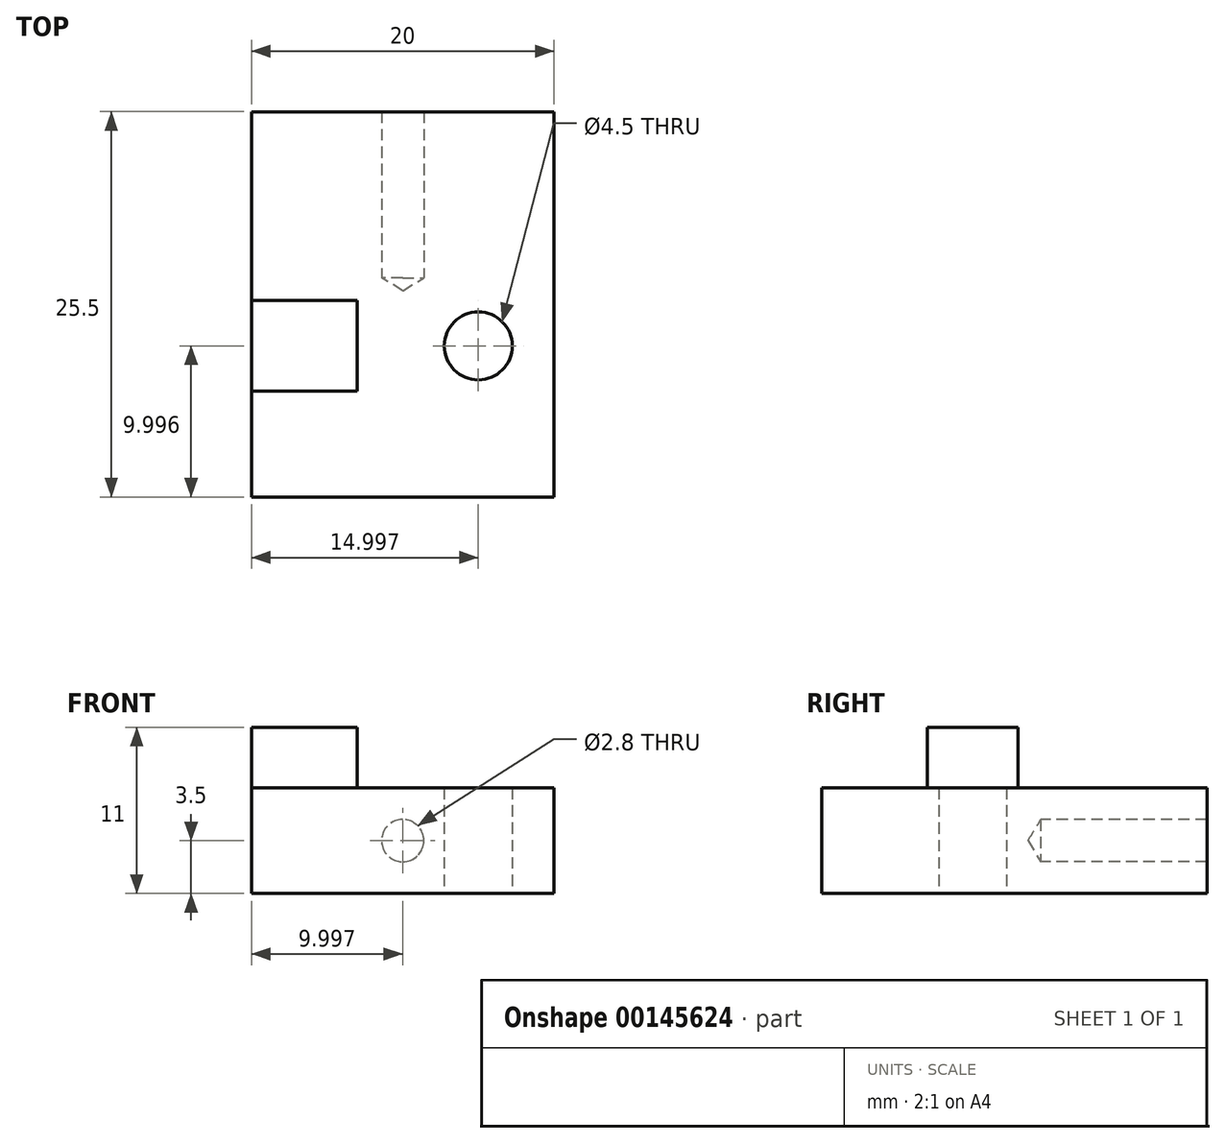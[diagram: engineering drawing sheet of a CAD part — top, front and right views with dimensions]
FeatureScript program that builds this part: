
annotation { "Feature Type Name" : "Feature", "Feature Type Description" : "" }
export const myFeature = defineFeature(function(context is Context, id is Id, definition is map)
    precondition{}
    {
        {
            var Q0;
            Q0=qCreatedBy(makeId("Top.planeOp"),FACE);
            var sketch = newSketch(context, id + "F0", { "sketchPlane" : qUnion([Q0])});
            skLineSegment(sketch, "E0.bottom", {"start": v(-42.58, 30.69) * mm, "end": v(-22.58, 30.69) * mm});
            skLineSegment(sketch, "E0.top", {"start": v(-42.58, 5.19) * mm, "end": v(-22.58, 5.19) * mm});
            skLineSegment(sketch, "E0.left", {"start": v(-42.58, 30.69) * mm, "end": v(-42.58, 5.19) * mm});
            skLineSegment(sketch, "E0.right", {"start": v(-22.58, 30.69) * mm, "end": v(-22.58, 5.19) * mm});
            skLineSegment(sketch, "E1", {"start": v(-41.58, 15.19) * mm, "end": v(-22.96, 15.19) * mm, "construction": true});
            skPoint(sketch, "E2", {"position": v(-39.08, 15.19) * mm});
            skPoint(sketch, "E3", {"position": v(-27.58, 15.19) * mm});
            skLineSegment(sketch, "E4.bottom", {"start": v(-42.58, 18.19) * mm, "end": v(-35.58, 18.19) * mm});
            skLineSegment(sketch, "E4.top", {"start": v(-42.58, 12.19) * mm, "end": v(-35.58, 12.19) * mm});
            skLineSegment(sketch, "E4.left", {"start": v(-42.58, 18.19) * mm, "end": v(-42.58, 12.19) * mm});
            skLineSegment(sketch, "E4.right", {"start": v(-35.58, 18.19) * mm, "end": v(-35.58, 12.19) * mm});
            skCircle(sketch, "E5", {"center": v(-27.58, 15.19) * mm, "radius": 2.25 * mm});
            skSolve(sketch);
        }
        {
            var Q0;
            {var subQ4=sQuery(id+"F0.wireOp",EDGE,"E0.bottom");Q0=makeQuery(id+"F0.imprint","IMPRINT",FACE,{"disambiguationData":[TD([[makeQuery(id+"F0.imprint","IMPRINT",EDGE,{"derivedFrom":subQ4}),-1.0]])]});}
            extrude(context, id + "F1", {"entities" : qUnion([Q0]), "depth" : 7 * mm, "offsetDistance" : 25 * mm});
        }
        {
            var Q0;
            Q0=makeQuery(id+"F0.imprint","IMPRINT",FACE,{"disambiguationData":[TD([[makeQuery(id+"F0.imprint","IMPRINT",EDGE,{"derivedFrom":sQuery(id+"F0.wireOp",EDGE,"E4.bottom")}),-1.0]])]});
            extrude(context, id + "F2", {"entities" : qUnion([Q0]), "operationType" : NewBodyOperationType.ADD, "depth" : 11 * mm, "offsetDistance" : 25 * mm});
        }
        {
            var Q0;
            Q0=makeQuery(id+"F1.opExtrude","SWEPT_FACE",FACE,{"disambiguationData":[OSD([sQuery(id+"F0.wireOp",EDGE,"E0.bottom")])]});
            var sketch = newSketch(context, id + "F3", { "sketchPlane" : qUnion([Q0])});
            skLineSegment(sketch, "E6", {"start": v(42.58, 0) * mm, "end": v(22.58, 7) * mm, "construction": true});
            skPoint(sketch, "E7", {"position": v(32.58, 3.5) * mm});
            skSolve(sketch);
        }
        {
            var Q0;
            Q0=sQuery(id+"F3.wireOp",VERTEX,"E7");
            var Q1;
            Q1=makeQuery(id+"F1.opExtrude","SWEPT_BODY",BODY,{"disambiguationData":[OSD([sQuery(id+"F0.wireOp",EDGE,"E0.bottom"),sQuery(id+"F0.wireOp",EDGE,"E0.top"),sQuery(id+"F0.wireOp",EDGE,"E0.left"),sQuery(id+"F0.wireOp",EDGE,"E0.right"),sQuery(id+"F0.wireOp",EDGE,"E4.bottom"),sQuery(id+"F0.wireOp",EDGE,"E4.top"),sQuery(id+"F0.wireOp",EDGE,"E4.right"),sQuery(id+"F0.wireOp",EDGE,"E5")])]});
            hole(context, id + "F4", {"style" : HoleStyle.SIMPLE, "endStyle" : HoleEndStyle.BLIND, "holeDiameter" : 2.8 * mm, "majorDiameter" : 5 * mm, "holeDepth" : 11 * mm, "tappedDepth" : 30 * mm, "tapClearance" : 3, "startFromSketch" : true, "locations" : qUnion([Q0]), "scope" : qUnion([Q1])});
        }
    });
